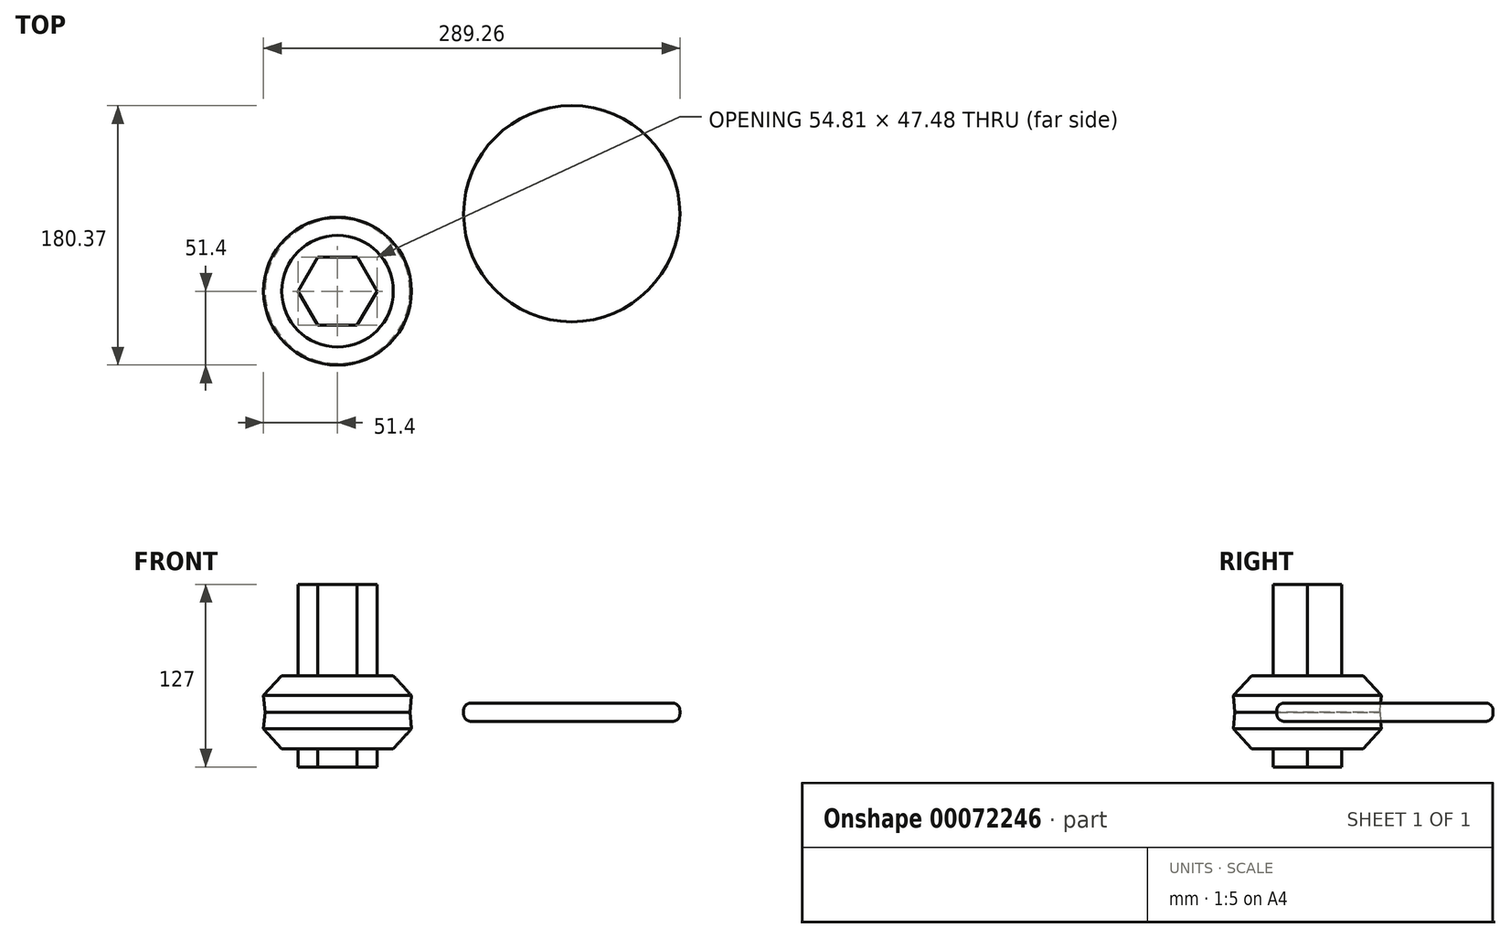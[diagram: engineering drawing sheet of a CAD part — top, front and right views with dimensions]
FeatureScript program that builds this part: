
annotation { "Feature Type Name" : "Feature", "Feature Type Description" : "" }
export const myFeature = defineFeature(function(context is Context, id is Id, definition is map)
    precondition{}
    {
        {
            var Q0;
            Q0=qCreatedBy(makeId("Top.planeOp"),FACE);
            var sketch = newSketch(context, id + "F0", { "sketchPlane" : qUnion([Q0])});
            skCircle(sketch, "E0", {"center": v(0, 0) * mm, "radius": 50.39 * mm});
            skCircle(sketch, "E1", {"center": v(162.74, 53.86) * mm, "radius": 75.12 * mm});
            skSolve(sketch);
        }
        {
            var Q0;
            Q0=makeQuery(id+"F0.imprint","IMPRINT",FACE,{"disambiguationData":[TD([[makeQuery(id+"F0.imprint","IMPRINT",EDGE,{"derivedFrom":sQuery(id+"F0.wireOp",EDGE,"E0")}),1.0]])]});
            extrude(context, id + "F1", {"entities" : qUnion([Q0]), "endBound" : BoundingType.SYMMETRIC, "depth" : 50.8 * mm, "hasDraft" : true, "draftAngle" : 5 * degree});
        }
        {
            var Q0;
            Q0=makeQuery(id+"F0.imprint","IMPRINT",FACE,{"disambiguationData":[TD([[makeQuery(id+"F0.imprint","IMPRINT",EDGE,{"derivedFrom":sQuery(id+"F0.wireOp",EDGE,"E1")}),1.0]])]});
            extrude(context, id + "F2", {"entities" : qUnion([Q0]), "endBound" : BoundingType.SYMMETRIC, "depth" : 12.7 * mm});
        }
        {
            var Q0;
            Q0=makeQuery(id+"F1.opExtrude","CAP_FACE",FACE,{"disambiguationData":[OSD([sQuery(id+"F0.wireOp",EDGE,"E0")])],"isStart":false});
            var sketch = newSketch(context, id + "F3", { "sketchPlane" : qUnion([Q0])});
            skCircle(sketch, "E2.cCircle", {"center": v(0, 0) * mm, "radius": 23.73 * mm, "construction": true});
            skLineSegment(sketch, "E2.0", {"start": v(-27.4, 0.01) * mm, "end": v(-13.7, 23.74) * mm});
            skLineSegment(sketch, "E2.1", {"start": v(-13.7, 23.74) * mm, "end": v(13.71, 23.73) * mm});
            skLineSegment(sketch, "E2.2", {"start": v(13.71, 23.73) * mm, "end": v(27.4, -0.01) * mm});
            skLineSegment(sketch, "E2.3", {"start": v(27.4, -0.01) * mm, "end": v(13.7, -23.74) * mm});
            skLineSegment(sketch, "E2.4", {"start": v(13.7, -23.74) * mm, "end": v(-13.71, -23.73) * mm});
            skLineSegment(sketch, "E2.5", {"start": v(-13.71, -23.73) * mm, "end": v(-27.4, 0.01) * mm});
            skPoint(sketch, "E2.0.midPoint", {"position": v(-20.55, 11.87) * mm});
            skSolve(sketch);
        }
        {
            var Q0;
            Q0=makeQuery(id+"F3.imprint","IMPRINT",FACE,{"disambiguationData":[TD([[makeQuery(id+"F3.imprint","IMPRINT",EDGE,{"derivedFrom":sQuery(id+"F3.wireOp",EDGE,"E2.0")}),-1.0]])]});
            extrude(context, id + "F4", {"entities" : qUnion([Q0]), "operationType" : NewBodyOperationType.ADD, "endBound" : BoundingType.SYMMETRIC, "oppositeDirection" : true, "depth" : 127 * mm});
        }
        {
            var Q0;
            Q0=makeQuery(id+"F1.opExtrude","CAP_EDGE",EDGE,{"disambiguationData":[OSD([sQuery(id+"F0.wireOp",EDGE,"E0")])],"isStart":false});
            var Q1;
            Q1=makeQuery(id+"F1.opExtrude","CAP_EDGE",EDGE,{"disambiguationData":[OSD([sQuery(id+"F0.wireOp",EDGE,"E0")])],"isStart":true});
            chamfer(context, id + "F5", {"entities" : qUnion([Q0, Q1]), "width" : 12.7 * mm, "tangentPropagation" : true});
        }
        {
            var Q0;
            Q0=makeQuery(id+"F2.opExtrude","CAP_EDGE",EDGE,{"disambiguationData":[OSD([sQuery(id+"F0.wireOp",EDGE,"E1")])],"isStart":true});
            var Q1;
            Q1=makeQuery(id+"F2.opExtrude","CAP_EDGE",EDGE,{"disambiguationData":[OSD([sQuery(id+"F0.wireOp",EDGE,"E1")])],"isStart":false});
            fillet(context, id + "F6", {"entities" : qUnion([Q0, Q1]), "radius" : 5.08 * mm, "tangentPropagation" : true, "allowEdgeOverflow" : false});
        }
    });
